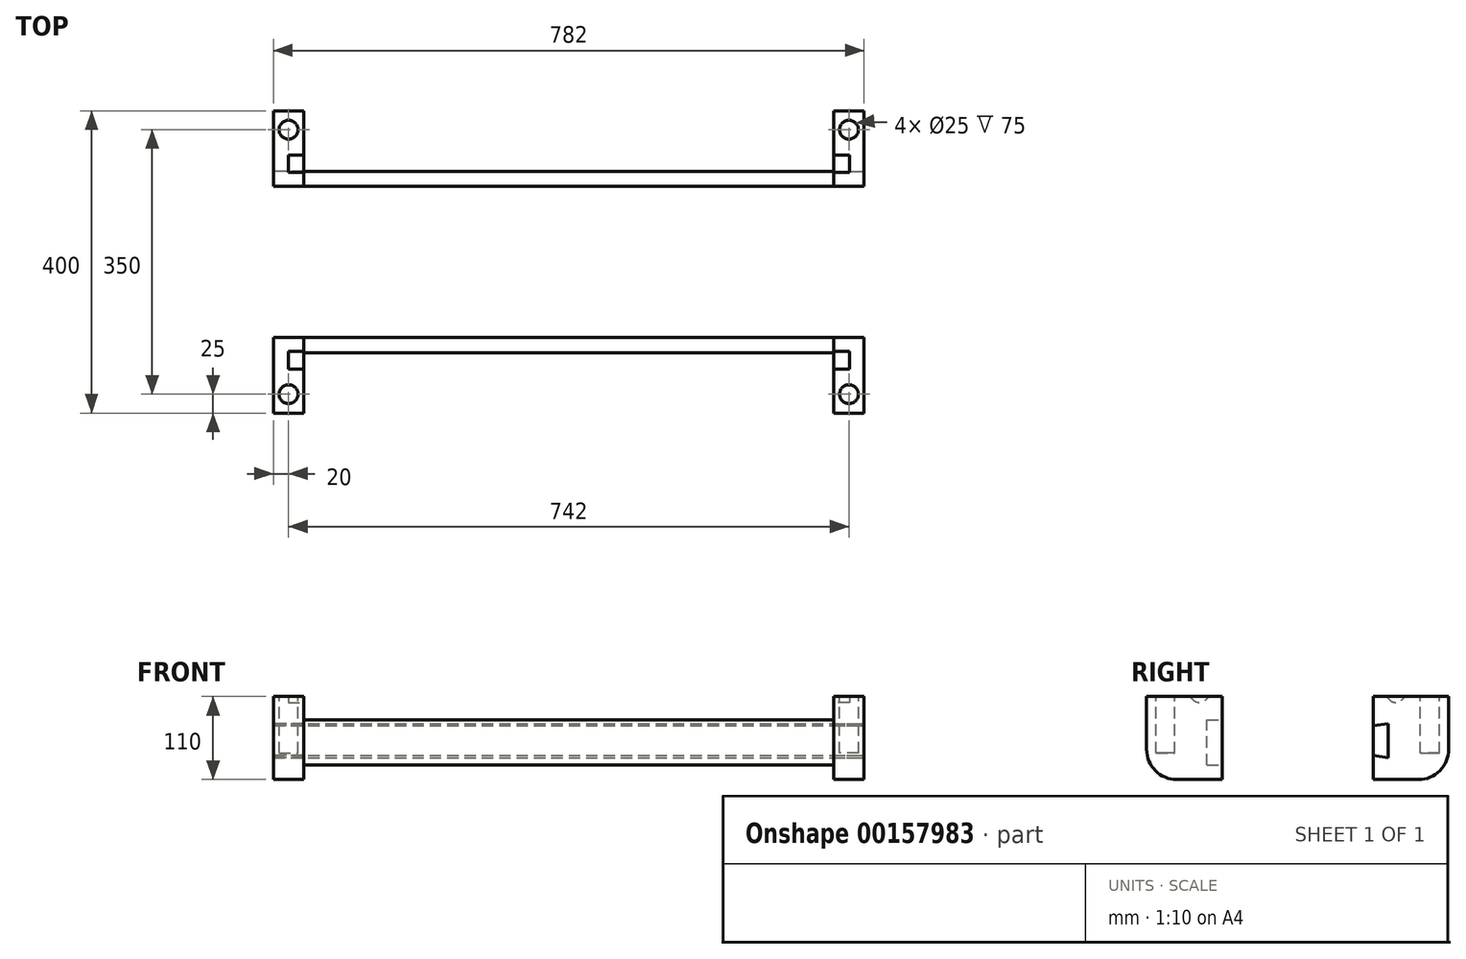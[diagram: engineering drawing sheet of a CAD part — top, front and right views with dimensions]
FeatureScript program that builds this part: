
annotation { "Feature Type Name" : "Feature", "Feature Type Description" : "" }
export const myFeature = defineFeature(function(context is Context, id is Id, definition is map)
    precondition{}
    {
        {
            var Q0;
            Q0=qCreatedBy(makeId("Right.planeOp"),FACE);
            var sketch = newSketch(context, id + "F0", { "sketchPlane" : qUnion([Q0])});
            skLineSegment(sketch, "E0.bottom", {"start": v(0, 0) * mm, "end": v(60, 0) * mm});
            skLineSegment(sketch, "E0.top", {"start": v(0, 110) * mm, "end": v(100, 110) * mm});
            skLineSegment(sketch, "E0.left", {"start": v(0, 0) * mm, "end": v(0, 110) * mm});
            skLineSegment(sketch, "E0.right", {"start": v(100, 40) * mm, "end": v(100, 110) * mm});
            skPoint(sketch, "E1.visualSharp", {"position": v(100, 0) * mm});
            skArc(sketch, "E1.filletArc", {"start": v(60, 0) * mm, "mid": v(88.28, 11.72) * mm, "end": v(100, 40) * mm});
            skSolve(sketch);
        }
        {
            var Q0;
            Q0 = qSketchRegion(id + "F0", true);
            extrude(context, id + "F1", {"entities" : qUnion([Q0]), "depth" : 40 * mm});
        }
        {
            var Q0;
            Q0=makeQuery(id+"F1.opExtrude","SWEPT_FACE",FACE,{"disambiguationData":[OSD([sQuery(id+"F0.wireOp",EDGE,"E0.top")])]});
            var sketch = newSketch(context, id + "F2", { "sketchPlane" : qUnion([Q0])});
            skCircle(sketch, "E2", {"center": v(20, 75) * mm, "radius": 12.5 * mm});
            skSolve(sketch);
        }
        {
            var Q0;
            Q0 = qSketchRegion(id + "F2", true);
            extrude(context, id + "F3", {"entities" : qUnion([Q0]), "operationType" : NewBodyOperationType.REMOVE, "oppositeDirection" : true, "depth" : 75 * mm});
        }
        {
            var Q0;
            Q0=makeQuery(id+"F1.opExtrude","CAP_FACE",FACE,{"disambiguationData":[OSD([sQuery(id+"F0.wireOp",EDGE,"E0.bottom"),sQuery(id+"F0.wireOp",EDGE,"E0.top"),sQuery(id+"F0.wireOp",EDGE,"E0.left"),sQuery(id+"F0.wireOp",EDGE,"E0.right"),sQuery(id+"F0.wireOp",EDGE,"E1.filletArc")])],"isStart":true});
            var sketch = newSketch(context, id + "F4", { "sketchPlane" : qUnion([Q0])});
            skCircle(sketch, "E3", {"center": v(-30, 114.5) * mm, "radius": 12.5 * mm});
            skSolve(sketch);
        }
        {
            var Q0;
            Q0 = qSketchRegion(id + "F4", true);
            extrude(context, id + "F5", {"entities" : qUnion([Q0]), "operationType" : NewBodyOperationType.REMOVE, "oppositeDirection" : true, "depth" : 20.5 * mm});
        }
        {
            var Q0;
            Q0=makeQuery(id+"F1.opExtrude","CAP_FACE",FACE,{"disambiguationData":[OSD([sQuery(id+"F0.wireOp",EDGE,"E0.bottom"),sQuery(id+"F0.wireOp",EDGE,"E0.top"),sQuery(id+"F0.wireOp",EDGE,"E0.left"),sQuery(id+"F0.wireOp",EDGE,"E0.right"),sQuery(id+"F0.wireOp",EDGE,"E1.filletArc")])],"isStart":false});
            var sketch = newSketch(context, id + "F6", { "sketchPlane" : qUnion([Q0])});
            skLineSegment(sketch, "E4", {"start": v(0, 71.41) * mm, "end": v(20, 74.22) * mm});
            skLineSegment(sketch, "E5", {"start": v(20, 74.22) * mm, "end": v(20, 46.78) * mm});
            skLineSegment(sketch, "E6", {"start": v(0, 56.41) * mm, "end": v(0, 71.41) * mm});
            skLineSegment(sketch, "E7.MirrorCS", {"start": v(20, 28.97) * mm, "end": v(20, 56.41) * mm});
            skLineSegment(sketch, "E8.MirrorCS", {"start": v(0, 31.78) * mm, "end": v(20, 28.97) * mm});
            skLineSegment(sketch, "E9.MirrorCS", {"start": v(0, 56.41) * mm, "end": v(0, 31.78) * mm});
            skSolve(sketch);
        }
        {
            var Q0;
            Q0 = qSketchRegion(id + "F6", true);
            extrude(context, id + "F7", {"entities" : qUnion([Q0]), "operationType" : NewBodyOperationType.REMOVE, "endBound" : BoundingType.THROUGH_ALL, "oppositeDirection" : true, "depth" : 25 * mm});
        }
        {
            var Q0;
            Q0=qCreatedBy(makeId("Right.planeOp"),FACE);
            cPlane(context, id + "F8", {"entities" : qUnion([Q0]), "cplaneType" : CPlaneType.OFFSET, "offset" : 351 * mm, "oppositeDirection" : true, "width" : 150 * mm, "height" : 150 * mm});
        }
        {
            var Q0;
            Q0=makeQuery(id+"F1.opExtrude","SWEPT_BODY",BODY,{"disambiguationData":[OSD([sQuery(id+"F0.wireOp",EDGE,"E0.bottom"),sQuery(id+"F0.wireOp",EDGE,"E0.top"),sQuery(id+"F0.wireOp",EDGE,"E0.left"),sQuery(id+"F0.wireOp",EDGE,"E0.right"),sQuery(id+"F0.wireOp",EDGE,"E1.filletArc")])]});
            var Q1;
            Q1=qCreatedBy(id+"F8.planeOp",FACE);
            mirror(context, id + "F9", {"entities" : qUnion([Q0]), "mirrorPlane" : qUnion([Q1])});
        }
        {
            var Q0;
            Q0=makeQuery(id+"F6.imprint","IMPRINT",FACE,{"disambiguationData":[TD([[makeQuery(id+"F6.imprint","IMPRINT",EDGE,{"derivedFrom":sQuery(id+"F6.wireOp",EDGE,"E4")}),-1.0]])]});
            extrude(context, id + "F10", {"entities" : qUnion([Q0]), "oppositeDirection" : true, "depth" : 782 * mm});
        }
        {
            var Q0;
            Q0=qCreatedBy(makeId("Front.planeOp"),FACE);
            cPlane(context, id + "F11", {"entities" : qUnion([Q0]), "cplaneType" : CPlaneType.OFFSET, "offset" : 100 * mm, "width" : 150 * mm, "height" : 150 * mm});
        }
        {
            var Q0;
            Q0=makeQuery(id+"F1.opExtrude","SWEPT_BODY",BODY,{"disambiguationData":[OSD([sQuery(id+"F0.wireOp",EDGE,"E0.bottom"),sQuery(id+"F0.wireOp",EDGE,"E0.top"),sQuery(id+"F0.wireOp",EDGE,"E0.left"),sQuery(id+"F0.wireOp",EDGE,"E0.right"),sQuery(id+"F0.wireOp",EDGE,"E1.filletArc")])]});
            var Q1;
            Q1=makeQuery(id+"F10.opExtrude","SWEPT_BODY",BODY,{"disambiguationData":[OSD([sQuery(id+"F6.wireOp",EDGE,"E4"),sQuery(id+"F6.wireOp",EDGE,"E5"),sQuery(id+"F6.wireOp",EDGE,"E6"),sQuery(id+"F6.wireOp",EDGE,"E7.MirrorCS"),sQuery(id+"F6.wireOp",EDGE,"E8.MirrorCS"),sQuery(id+"F6.wireOp",EDGE,"E9.MirrorCS")])]});
            var Q2;
            Q2=makeQuery(id+"F9.opPattern","COPY",BODY,{"derivedFrom":makeQuery(id+"F1.opExtrude","SWEPT_BODY",BODY,{"disambiguationData":[OSD([sQuery(id+"F0.wireOp",EDGE,"E0.bottom"),sQuery(id+"F0.wireOp",EDGE,"E0.top"),sQuery(id+"F0.wireOp",EDGE,"E0.left"),sQuery(id+"F0.wireOp",EDGE,"E0.right"),sQuery(id+"F0.wireOp",EDGE,"E1.filletArc")])]}),"instanceName":"1"});
            var Q3;
            Q3=qCreatedBy(id+"F11.planeOp",FACE);
            mirror(context, id + "F12", {"entities" : qUnion([Q0, Q1, Q2]), "mirrorPlane" : qUnion([Q3])});
        }
        {
            var Q0;
            Q0=qCreatedBy(makeId("Top.planeOp"),FACE);
            var Q1;
            Q1=makeQuery(id+"F12.opPattern","COPY",VERTEX,{"derivedFrom":makeQuery(id+"F9.opPattern","COPY",VERTEX,{"derivedFrom":makeQuery(id+"F7.boolean.opBoolean","INTERSECT",VERTEX,{"derivedFrom":[makeQuery(id+"F1.opExtrude","CAP_FACE",FACE,{"disambiguationData":[OSD([sQuery(id+"F0.wireOp",EDGE,"E0.bottom"),sQuery(id+"F0.wireOp",EDGE,"E0.top"),sQuery(id+"F0.wireOp",EDGE,"E0.left"),sQuery(id+"F0.wireOp",EDGE,"E0.right"),sQuery(id+"F0.wireOp",EDGE,"E1.filletArc")])],"isStart":true}),makeQuery(id+"F7.opExtrude","SWEPT_FACE",FACE,{"disambiguationData":[OSD([sQuery(id+"F6.wireOp",EDGE,"E4")])]}),makeQuery(id+"F7.opExtrude","SWEPT_FACE",FACE,{"disambiguationData":[OSD([sQuery(id+"F6.wireOp",EDGE,"E5"),sQuery(id+"F6.wireOp",EDGE,"E7.MirrorCS")])]})]}),"instanceName":"1"}),"instanceName":"1"});
            cPlane(context, id + "F13", {"entities" : qUnion([Q0, Q1]), "cplaneType" : CPlaneType.PLANE_POINT, "offset" : 25 * mm, "width" : 150 * mm, "height" : 150 * mm});
        }
        {
            var Q0;
            Q0=qCreatedBy(id+"F13.planeOp",FACE);
            var sketch = newSketch(context, id + "F14", { "sketchPlane" : qUnion([Q0])});
            skLineSegment(sketch, "E10.bottom", {"start": v(-702, -220) * mm, "end": v(0, -220) * mm});
            skLineSegment(sketch, "E10.top", {"start": v(-702, -200) * mm, "end": v(0, -200) * mm});
            skLineSegment(sketch, "E10.left", {"start": v(-702, -220) * mm, "end": v(-702, -200) * mm});
            skLineSegment(sketch, "E10.right", {"start": v(0, -220) * mm, "end": v(0, -200) * mm});
            skSolve(sketch);
        }
        {
            var Q0;
            Q0=makeQuery(id+"F14.imprint","IMPRINT",FACE,{"disambiguationData":[TD([[makeQuery(id+"F14.imprint","IMPRINT",EDGE,{"derivedFrom":sQuery(id+"F14.wireOp",EDGE,"E10.bottom")}),1.0]])]});
            extrude(context, id + "F15", {"entities" : qUnion([Q0]), "operationType" : NewBodyOperationType.ADD, "oppositeDirection" : true, "depth" : 55 * mm, "hasSecondDirection" : true, "secondDirectionOppositeDirection" : false, "secondDirectionDepth" : 5 * mm});
        }
    });
